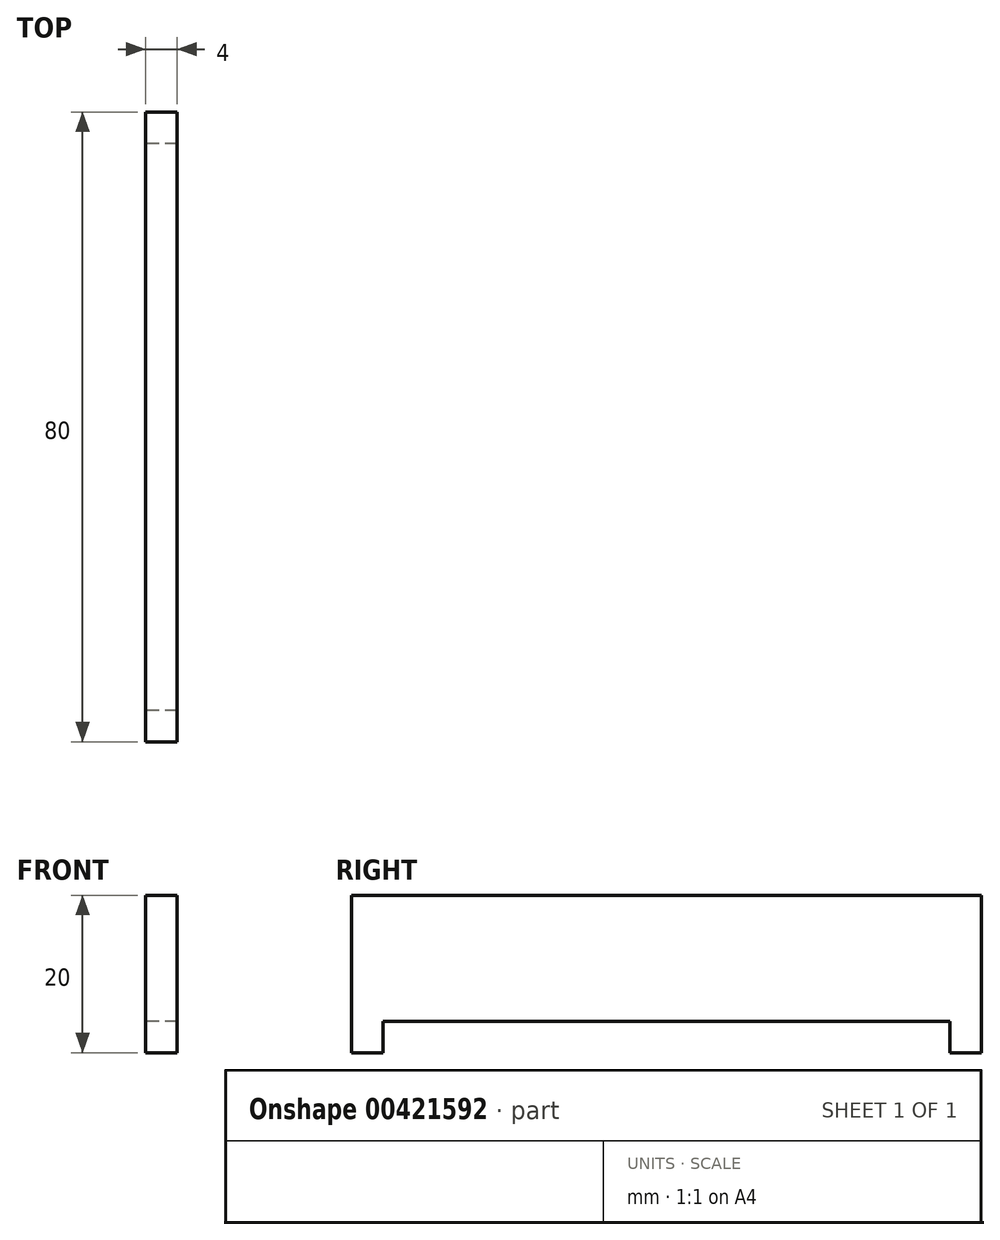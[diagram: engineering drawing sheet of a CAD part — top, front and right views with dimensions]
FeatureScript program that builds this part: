
annotation { "Feature Type Name" : "Feature", "Feature Type Description" : "" }
export const myFeature = defineFeature(function(context is Context, id is Id, definition is map)
    precondition{}
    {
        {
            var Q0;
            Q0=qCreatedBy(makeId("Right.planeOp"),FACE);
            var sketch = newSketch(context, id + "F0", { "sketchPlane" : qUnion([Q0])});
            skLineSegment(sketch, "E0", {"start": v(51, 13.75) * mm, "end": v(51, -6.25) * mm});
            skLineSegment(sketch, "E1", {"start": v(51, -6.25) * mm, "end": v(47, -6.25) * mm});
            skLineSegment(sketch, "E2", {"start": v(47, -6.25) * mm, "end": v(47, -2.25) * mm});
            skLineSegment(sketch, "E3", {"start": v(47, -2.25) * mm, "end": v(-25, -2.25) * mm});
            skLineSegment(sketch, "E4", {"start": v(-25, -2.25) * mm, "end": v(-25, -6.25) * mm});
            skLineSegment(sketch, "E5", {"start": v(-25, -6.25) * mm, "end": v(-29, -6.25) * mm});
            skLineSegment(sketch, "E6", {"start": v(-29, 13.75) * mm, "end": v(-29, -6.25) * mm});
            skLineSegment(sketch, "E7", {"start": v(-29, 13.75) * mm, "end": v(51, 13.75) * mm});
            skSolve(sketch);
        }
        {
            var Q0;
            Q0=makeQuery(id+"F0.imprint","IMPRINT",FACE,{"disambiguationData":[TD([[makeQuery(id+"F0.imprint","IMPRINT",EDGE,{"derivedFrom":sQuery(id+"F0.wireOp",EDGE,"E0")}),-1.0]])]});
            extrude(context, id + "F1", {"entities" : qUnion([Q0]), "depth" : 4 * mm, "offsetDistance" : 25 * mm});
        }
    });
